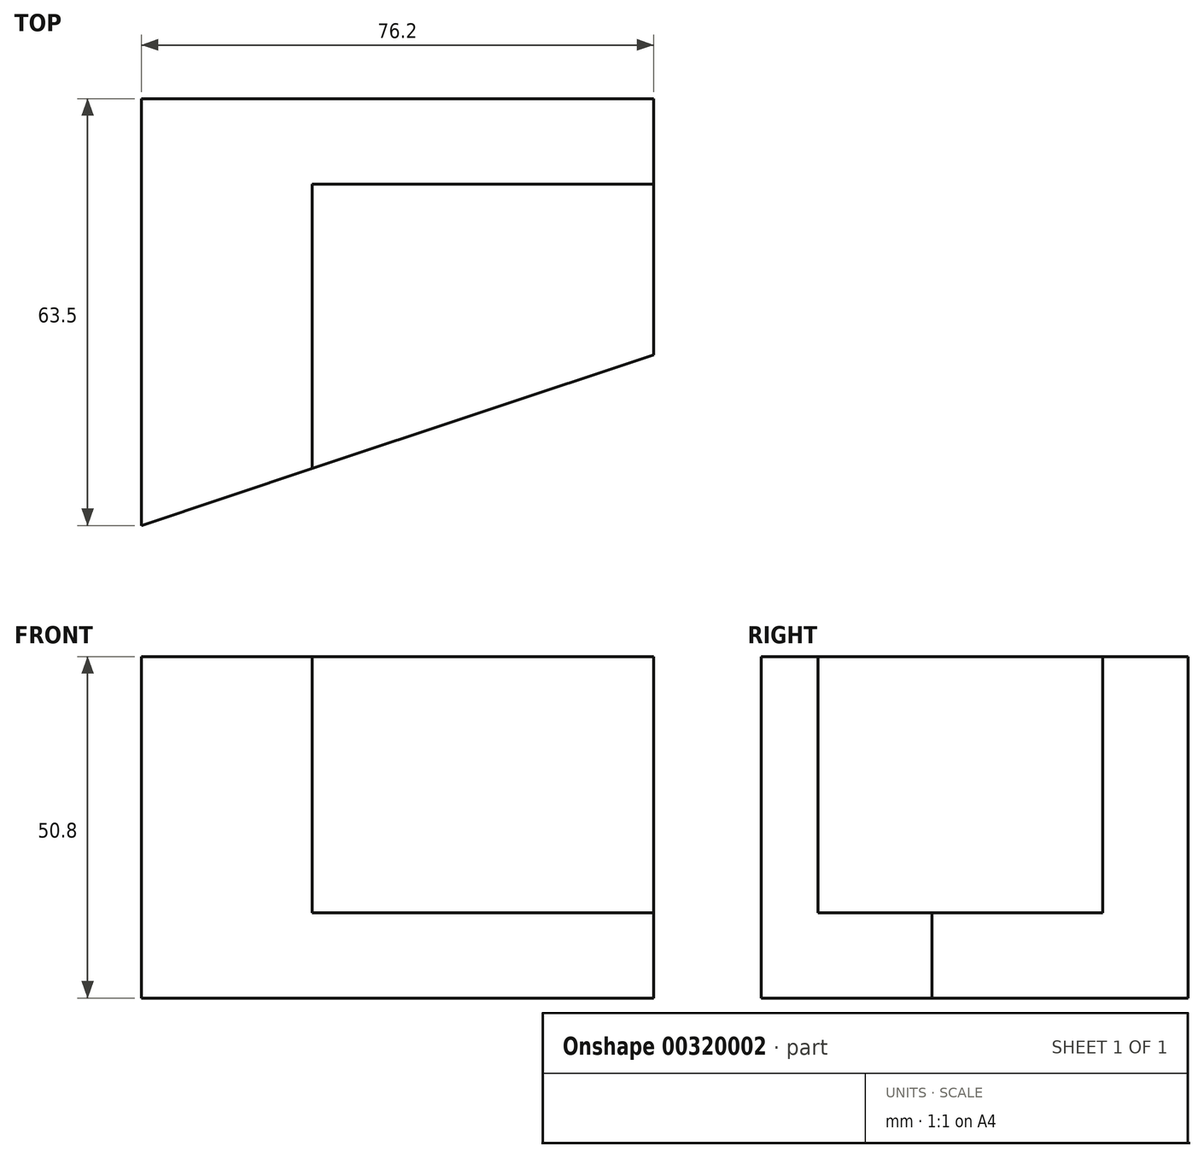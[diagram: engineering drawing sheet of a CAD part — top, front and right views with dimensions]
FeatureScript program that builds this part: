
annotation { "Feature Type Name" : "Feature", "Feature Type Description" : "" }
export const myFeature = defineFeature(function(context is Context, id is Id, definition is map)
    precondition{}
    {
        {
            var Q0;
            Q0=qCreatedBy(makeId("Front.planeOp"),FACE);
            var sketch = newSketch(context, id + "F0", { "sketchPlane" : qUnion([Q0])});
            skLineSegment(sketch, "E0.bottom", {"start": v(0, 0) * mm, "end": v(76.2, 0) * mm});
            skLineSegment(sketch, "E0.top", {"start": v(0, 50.8) * mm, "end": v(76.2, 50.8) * mm});
            skLineSegment(sketch, "E0.left", {"start": v(0, 0) * mm, "end": v(0, 50.8) * mm});
            skLineSegment(sketch, "E0.right", {"start": v(76.2, 0) * mm, "end": v(76.2, 50.8) * mm});
            skSolve(sketch);
        }
        {
            var Q0;
            Q0 = qSketchRegion(id + "F0", true);
            extrude(context, id + "F1", {"entities" : qUnion([Q0]), "oppositeDirection" : true, "depth" : 63.5 * mm});
        }
        {
            var Q0;
            Q0=makeQuery(id+"F1.opExtrude","CAP_FACE",FACE,{"disambiguationData":[OSD([sQuery(id+"F0.wireOp",EDGE,"E0.bottom"),sQuery(id+"F0.wireOp",EDGE,"E0.top"),sQuery(id+"F0.wireOp",EDGE,"E0.left"),sQuery(id+"F0.wireOp",EDGE,"E0.right")])],"isStart":true});
            var sketch = newSketch(context, id + "F2", { "sketchPlane" : qUnion([Q0])});
            skLineSegment(sketch, "E1.bottom", {"start": v(76.2, 50.8) * mm, "end": v(25.4, 50.8) * mm});
            skLineSegment(sketch, "E1.top", {"start": v(76.2, 12.7) * mm, "end": v(25.4, 12.7) * mm});
            skLineSegment(sketch, "E1.left", {"start": v(76.2, 50.8) * mm, "end": v(76.2, 12.7) * mm});
            skLineSegment(sketch, "E1.right", {"start": v(25.4, 50.8) * mm, "end": v(25.4, 12.7) * mm});
            skSolve(sketch);
        }
        {
            var Q0;
            Q0 = qSketchRegion(id + "F2", true);
            extrude(context, id + "F3", {"entities" : qUnion([Q0]), "operationType" : NewBodyOperationType.REMOVE, "oppositeDirection" : true, "depth" : 50.8 * mm});
        }
        {
            var Q0;
            Q0=makeQuery(id+"F1.opExtrude","SWEPT_FACE",FACE,{"disambiguationData":[OSD([sQuery(id+"F0.wireOp",EDGE,"E0.bottom")])]});
            var sketch = newSketch(context, id + "F4", { "sketchPlane" : qUnion([Q0])});
            skLineSegment(sketch, "E2", {"start": v(76.2, 0) * mm, "end": v(76.2, -25.4) * mm});
            skLineSegment(sketch, "E3", {"start": v(76.2, -25.4) * mm, "end": v(0, 0) * mm});
            skLineSegment(sketch, "E4", {"start": v(76.2, 0) * mm, "end": v(0, 0) * mm});
            skSolve(sketch);
        }
        {
            var Q0;
            Q0 = qSketchRegion(id + "F4", true);
            extrude(context, id + "F5", {"entities" : qUnion([Q0]), "operationType" : NewBodyOperationType.REMOVE, "endBound" : BoundingType.THROUGH_ALL, "oppositeDirection" : true, "depth" : 25.4 * mm});
        }
    });
